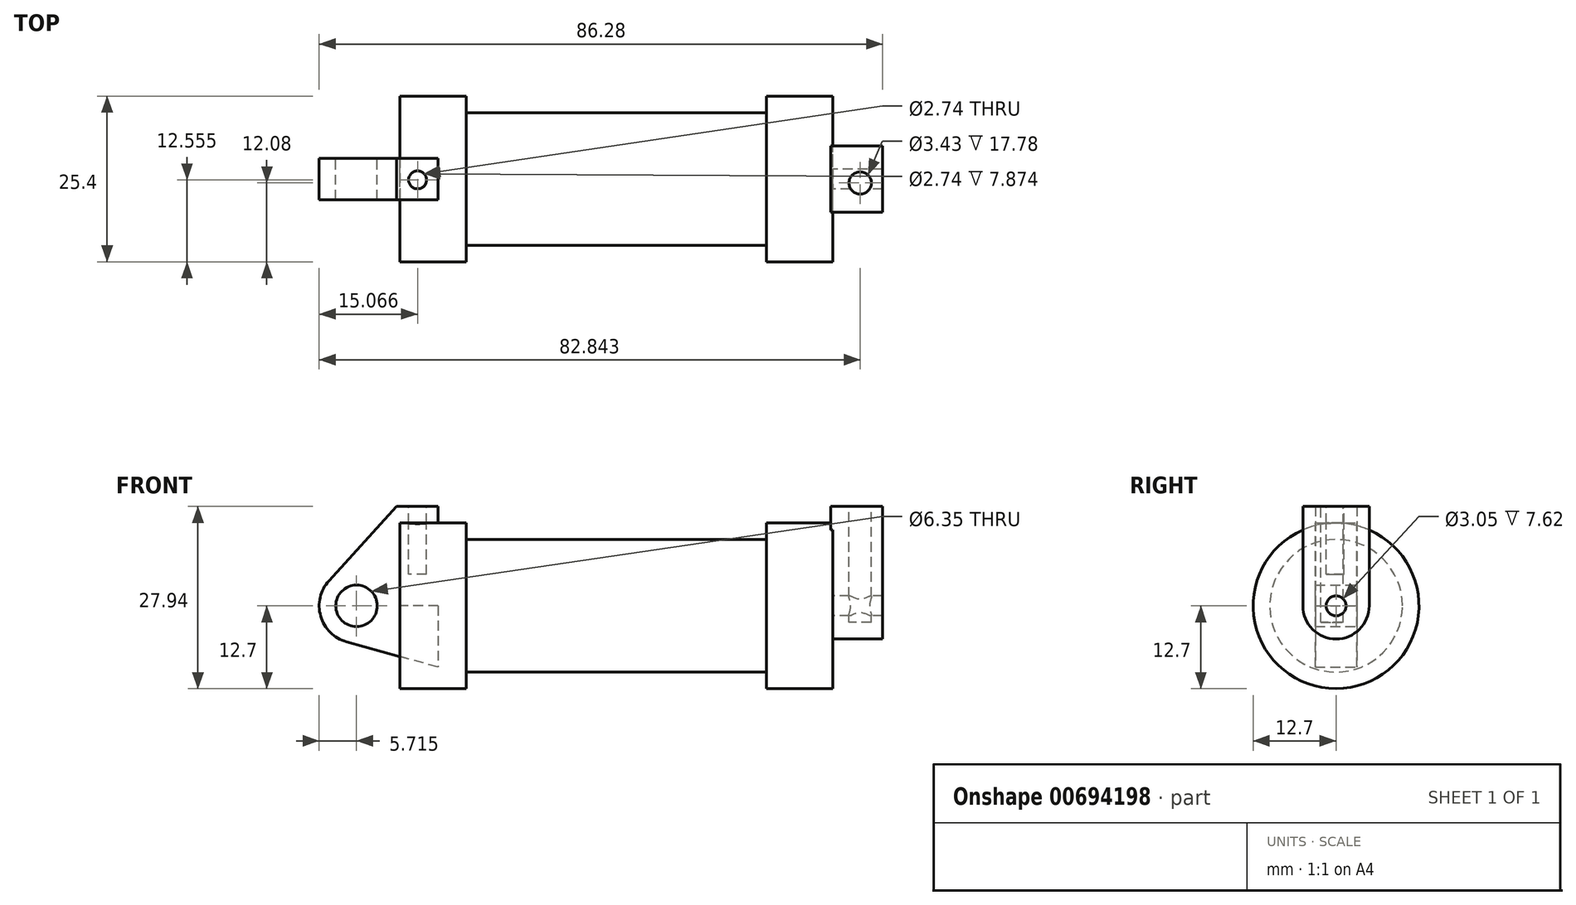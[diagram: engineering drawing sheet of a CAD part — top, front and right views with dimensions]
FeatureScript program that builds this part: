
annotation { "Feature Type Name" : "Feature", "Feature Type Description" : "" }
export const myFeature = defineFeature(function(context is Context, id is Id, definition is map)
    precondition{}
    {
        {
            var Q0;
            Q0=qCreatedBy(makeId("Front.planeOp"),FACE);
            var sketch = newSketch(context, id + "F0", { "sketchPlane" : qUnion([Q0])});
            skLineSegment(sketch, "E0", {"start": v(0, 0) * mm, "end": v(0, 12.7) * mm});
            skLineSegment(sketch, "E1", {"start": v(0, 12.7) * mm, "end": v(10.16, 12.7) * mm});
            skLineSegment(sketch, "E2", {"start": v(10.16, 12.7) * mm, "end": v(10.16, 10.16) * mm});
            skLineSegment(sketch, "E3", {"start": v(10.16, 10.16) * mm, "end": v(56.13, 10.16) * mm});
            skLineSegment(sketch, "E4", {"start": v(56.13, 10.16) * mm, "end": v(56.13, 12.7) * mm});
            skLineSegment(sketch, "E5", {"start": v(56.13, 12.7) * mm, "end": v(66.3, 12.7) * mm});
            skLineSegment(sketch, "E6", {"start": v(66.3, 12.7) * mm, "end": v(66.3, 0) * mm});
            skLineSegment(sketch, "E7", {"start": v(66.3, 0) * mm, "end": v(0, 0) * mm});
            skLineSegment(sketch, "E8", {"start": v(5.84, 15.24) * mm, "end": v(-0.5, 15.24) * mm});
            skLineSegment(sketch, "E9", {"start": v(-0.5, 15.24) * mm, "end": v(-10.88, 3.85) * mm});
            skLineSegment(sketch, "E10", {"start": v(0, 0) * mm, "end": v(-6.65, 0) * mm});
            skCircle(sketch, "E11", {"center": v(-6.65, 0) * mm, "radius": 5.72 * mm});
            skCircle(sketch, "E12", {"center": v(-6.65, 0) * mm, "radius": 3.18 * mm});
            skLineSegment(sketch, "E13", {"start": v(5.84, 15.24) * mm, "end": v(5.84, -9.4) * mm});
            skLineSegment(sketch, "E14", {"start": v(5.84, -9.4) * mm, "end": v(-8.18, -5.5) * mm});
            skSolve(sketch);
        }
        {
            var Q0;
            {var subQ0=sQuery(id+"F0.wireOp",EDGE,"E2");Q0=makeQuery(id+"F0.imprint","IMPRINT",FACE,{"disambiguationData":[TD([[makeQuery(id+"F0.imprint","IMPRINT",EDGE,{"derivedFrom":subQ0}),-1.0]])]});}
            var Q1;
            {var subQ0=sQuery(id+"F0.wireOp",EDGE,"E0");Q1=makeQuery(id+"F0.imprint","IMPRINT",FACE,{"disambiguationData":[TD([[makeQuery(id+"F0.imprint","IMPRINT",EDGE,{"derivedFrom":subQ0}),-1.0]])]});}
            var Q2;
            Q2=sQuery(id+"F0.wireOp",EDGE,"E7");
            revolve(context, id + "F1", {"entities" : qUnion([Q0, Q1]), "axis" : qUnion([Q2]), "revolveType" : RevolveType.FULL});
        }
        {
            var Q0;
            {var subQ1=sQuery(id+"F0.wireOp",EDGE,"E0");Q0=makeQuery(id+"F0.imprint","IMPRINT",FACE,{"disambiguationData":[TD([[makeQuery(id+"F0.imprint","IMPRINT",EDGE,{"derivedFrom":subQ1}),1.0]])]});}
            var Q1;
            {var subQ5=sQuery(id+"F0.wireOp",EDGE,"E12");Q1=makeQuery(id+"F0.imprint","IMPRINT",FACE,{"disambiguationData":[TD([[makeQuery(id+"F0.imprint","IMPRINT",EDGE,{"derivedFrom":subQ5}),-1.0]])]});}
            var Q2;
            {var subQ0=sQuery(id+"F0.wireOp",EDGE,"E14");Q2=makeQuery(id+"F0.imprint","IMPRINT",FACE,{"disambiguationData":[TD([[makeQuery(id+"F0.imprint","IMPRINT",EDGE,{"derivedFrom":subQ0}),-1.0]])]});}
            extrude(context, id + "F2", {"entities" : qUnion([Q0, Q1, Q2]), "endBound" : BoundingType.SYMMETRIC, "depth" : 6.35 * mm, "offsetDistance" : 25.4 * mm});
        }
        {
            var Q0;
            Q0=makeQuery(id+"F1.opRevolve","SWEPT_FACE",FACE,{"disambiguationData":[OSD([sQuery(id+"F0.wireOp",EDGE,"E6")])]});
            var sketch = newSketch(context, id + "F3", { "sketchPlane" : qUnion([Q0])});
            skCircle(sketch, "E15", {"center": v(0, 0) * mm, "radius": 5.08 * mm});
            skCircle(sketch, "E16", {"center": v(0, 0) * mm, "radius": 1.52 * mm});
            skLineSegment(sketch, "E17.bottom", {"start": v(-5.08, 15.24) * mm, "end": v(5.08, 15.24) * mm});
            skLineSegment(sketch, "E17.left", {"start": v(-5.08, 15.24) * mm, "end": v(-5.08, 0) * mm});
            skLineSegment(sketch, "E17.right", {"start": v(5.08, 15.24) * mm, "end": v(5.08, 0) * mm});
            skSolve(sketch);
        }
        {
            var Q0;
            {var subQ0=sQuery(id+"F3.wireOp",EDGE,"E17.bottom");Q0=makeQuery(id+"F3.imprint","IMPRINT",FACE,{"disambiguationData":[TD([[makeQuery(id+"F3.imprint","IMPRINT",EDGE,{"derivedFrom":subQ0}),-1.0]])]});}
            var Q1;
            {var subQ0=sQuery(id+"F3.wireOp",EDGE,"E17.left");var subQ1=sQuery(id+"F3.wireOp",EDGE,"E15");var subQ2=makeQuery(id+"F3.imprint","INTERSECT",VERTEX,{"derivedFrom":[subQ1,subQ0]});Q1=makeQuery(id+"F3.imprint","IMPRINT",FACE,{"disambiguationData":[TD([[makeQuery(id+"F3.imprint","IMPRINT",EDGE,{"disambiguationData":[TD([[subQ2,1.0]])],"derivedFrom":subQ1}),-1.0]])]});}
            var Q2;
            Q2=makeQuery(id+"F3.imprint","IMPRINT",FACE,{"disambiguationData":[TD([[makeQuery(id+"F3.imprint","IMPRINT",EDGE,{"derivedFrom":sQuery(id+"F3.wireOp",EDGE,"E16")}),-1.0]])]});
            extrude(context, id + "F4", {"entities" : qUnion([Q0, Q1, Q2]), "operationType" : NewBodyOperationType.ADD, "depth" : 7.62 * mm, "offsetDistance" : 25.4 * mm});
        }
        {
            var Q0;
            Q0 = qSketchRegion(id + "F3", true);
            extrude(context, id + "F5", {"entities" : qUnion([Q0]), "operationType" : NewBodyOperationType.ADD, "oppositeDirection" : true, "depth" : 0.3 * mm, "offsetDistance" : 25.4 * mm});
        }
        {
            var Q0;
            {var subQ0=sQuery(id+"F3.wireOp",EDGE,"E17.bottom");Q0=makeQuery(id+"F5.boolean.opBoolean","MERGE",FACE,{"derivedFrom":[makeQuery(id+"F4.opExtrude","SWEPT_FACE",FACE,{"disambiguationData":[OSD([subQ0])]}),makeQuery(id+"F5.opExtrude","SWEPT_FACE",FACE,{"disambiguationData":[OSD([subQ0])]})]});}
            var sketch = newSketch(context, id + "F6", { "sketchPlane" : qUnion([Q0])});
            skCircle(sketch, "E18", {"center": v(70.47, -0.62) * mm, "radius": 1.72 * mm});
            skSolve(sketch);
        }
        {
            var Q0;
            Q0 = qSketchRegion(id + "F6", true);
            extrude(context, id + "F7", {"entities" : qUnion([Q0]), "operationType" : NewBodyOperationType.REMOVE, "oppositeDirection" : true, "depth" : 17.78 * mm, "offsetDistance" : 25.4 * mm});
        }
        {
            var Q0;
            Q0=makeQuery(id+"F2.opExtrude","SWEPT_FACE",FACE,{"disambiguationData":[OSD([sQuery(id+"F0.wireOp",EDGE,"E8")])]});
            var sketch = newSketch(context, id + "F8", { "sketchPlane" : qUnion([Q0])});
            skCircle(sketch, "E19", {"center": v(2.7, -0.15) * mm, "radius": 1.37 * mm});
            skSolve(sketch);
        }
        {
            var Q0;
            Q0 = qSketchRegion(id + "F8", true);
            extrude(context, id + "F9", {"entities" : qUnion([Q0]), "operationType" : NewBodyOperationType.REMOVE, "oppositeDirection" : true, "depth" : 10.4 * mm, "offsetDistance" : 25.4 * mm});
        }
    });
